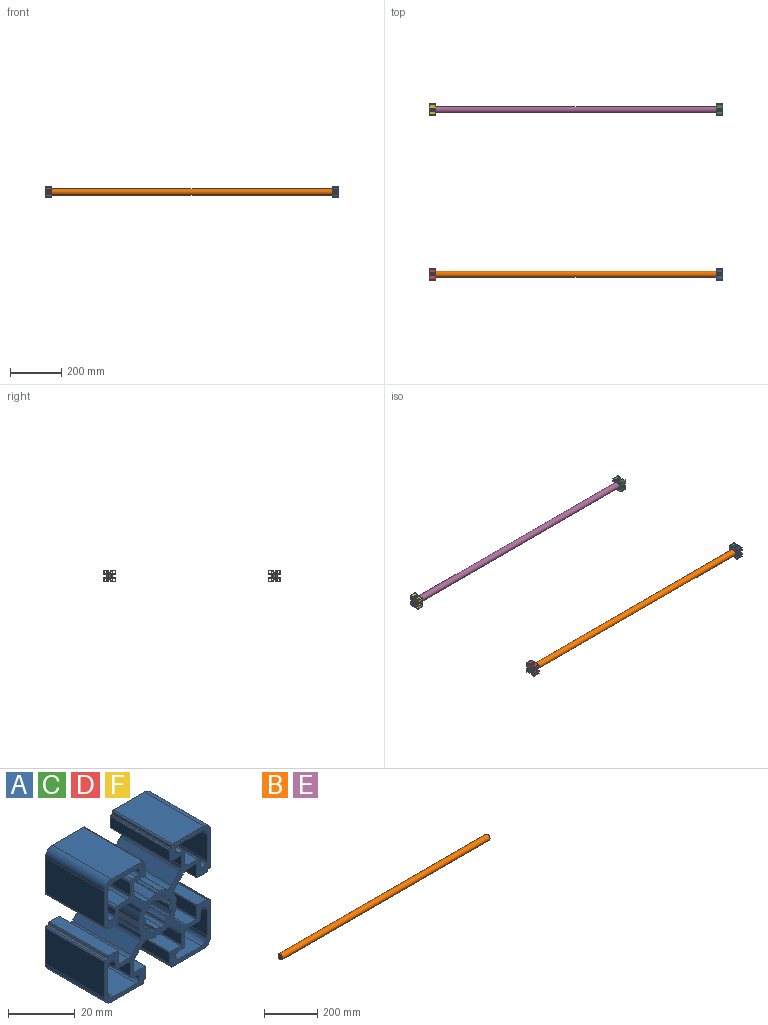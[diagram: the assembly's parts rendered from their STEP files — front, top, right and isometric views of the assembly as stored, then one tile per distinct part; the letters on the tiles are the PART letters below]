
ASSEMBLY  parts=6 mates=5
PART A: 246 faces, bbox 45x25x45 mm
  f0: plane 25x1.55mm, normal (0,0,1), area 38.7mm2, adj f1,f123,f244,f245
  f1: cylinder r=1mm len=25mm, axis (0,-1,0), area 39.3mm2, adj f0,f2,f244,f245
  f2: plane 25x4.45mm, normal (1,0,0), area 111.3mm2, adj f1,f3,f244,f245
  f3: cylinder r=1mm len=25mm, axis (0,-1,0), area 39.3mm2, adj f2,f4,f244,f245
  f4: plane 25x4.45mm, normal (0,0,1), area 111.3mm2, adj f3,f5,f244,f245
  f5: cylinder r=1mm len=25mm, axis (0,-1,0), area 39.3mm2, adj f4,f122,f244,f245
  f6: plane 25x1.55mm, normal (0,0,1), area 38.7mm2, adj f7,f129,f244,f245
  f7: cylinder r=1.5mm len=25mm, axis (0,-1,0), area 117.8mm2, adj f6,f8,f244,f245
  f8: plane 25x9.5mm, normal (0,0,-1), area 237.5mm2, adj f7,f9,f244,f245
  f9: cylinder r=2.5mm len=25mm, axis (0,-1,0), area 98.2mm2, adj f8,f10,f244,f245
  f10: plane 25x9.5mm, normal (1,0,0), area 237.5mm2, adj f9,f11,f244,f245
  f11: cylinder r=1.5mm len=25mm, axis (0,-1,0), area 117.8mm2, adj f10,f128,f244,f245
  f12: plane 25x9.5mm, normal (0,0,1), area 237.5mm2, adj f13,f135,f244,f245
  f13: cylinder r=1.5mm len=25mm, axis (0,-1,0), area 117.8mm2, adj f12,f14,f244,f245
  f14: plane 25x1.55mm, normal (0,0,-1), area 38.7mm2, adj f13,f15,f244,f245
  f15: cylinder r=1mm len=25mm, axis (0,-1,0), area 39.3mm2, adj f14,f16,f244,f245
  f16: plane 25x4.45mm, normal (-1,0,0), area 111.3mm2, adj f15,f17,f244,f245
  f17: cylinder r=1mm len=25mm, axis (0,-1,0), area 39.3mm2, adj f16,f134,f244,f245
  f18: plane 25x1.55mm, normal (0,0,-1), area 38.7mm2, adj f19,f141,f244,f245
  f19: cylinder r=1.5mm len=25mm, axis (0,-1,0), area 117.8mm2, adj f18,f20,f244,f245
  f20: plane 25x9.5mm, normal (0,0,1), area 237.5mm2, adj f19,f21,f244,f245
  f21: cylinder r=2.5mm len=25mm, axis (0,-1,0), area 98.2mm2, adj f20,f22,f244,f245
  f22: plane 25x9.5mm, normal (-1,0,0), area 237.5mm2, adj f21,f23,f244,f245
  f23: cylinder r=1.5mm len=25mm, axis (0,-1,0), area 117.8mm2, adj f22,f140,f244,f245
  f24: cylinder r=0.5mm len=25mm, axis (0,-1,0), area 21.3mm2, adj f25,f147,f244,f245
  f25: plane 25x0.46mm, normal (0.58,0,-0.82), area 14.2mm2, adj f24,f26,f244,f245
  f26: cylinder r=5mm len=25mm, axis (0,-1,0), area 43.5mm2, adj f25,f27,f244,f245
  f27: plane 25x0.48mm, normal (-0.82,0,0.57), area 14.5mm2, adj f26,f28,f244,f245
  f28: cylinder r=0.5mm len=25mm, axis (0,-1,0), area 21.2mm2, adj f27,f29,f244,f245
  f29: cylinder r=6.1mm len=25mm, axis (0,-1,0), area 39.3mm2, adj f28,f30,f244,f245
  f30: cylinder r=0.5mm len=25mm, axis (0,-1,0), area 21.3mm2, adj f29,f31,f244,f245
  f31: plane 25x0.57mm, normal (0.99,0,-0.17), area 14.4mm2, adj f30,f32,f244,f245
  f32: cylinder r=5mm len=25mm, axis (0,-1,0), area 44.6mm2, adj f31,f33,f244,f245
  f33: plane 25x0.57mm, normal (-0.99,0,-0.17), area 14.4mm2, adj f32,f34,f244,f245
  f34: cylinder r=0.5mm len=25mm, axis (0,-1,0), area 21.3mm2, adj f33,f35,f244,f245
  f35: cylinder r=6.1mm len=25mm, axis (0,-1,0), area 39.3mm2, adj f34,f36,f244,f245
  f36: cylinder r=0.5mm len=25mm, axis (0,-1,0), area 21.2mm2, adj f35,f37,f244,f245
  f37: plane 25x0.48mm, normal (0.82,0,0.57), area 14.5mm2, adj f36,f38,f244,f245
  f38: cylinder r=5mm len=25mm, axis (0,-1,0), area 43.5mm2, adj f37,f39,f244,f245
  f39: plane 25x0.46mm, normal (-0.58,0,-0.82), area 14.2mm2, adj f38,f40,f244,f245
  f40: cylinder r=0.5mm len=25mm, axis (0,-1,0), area 21.3mm2, adj f39,f41,f244,f245
  f41: cylinder r=6.1mm len=25mm, axis (0,-1,0), area 39.3mm2, adj f40,f42,f244,f245
  f42: cylinder r=0.5mm len=25mm, axis (0,-1,0), area 21.2mm2, adj f41,f43,f244,f245
  f43: plane 25x0.56mm, normal (0.18,0,0.98), area 14.1mm2, adj f42,f44,f244,f245
  f44: cylinder r=5mm len=25mm, axis (0,-1,0), area 43.6mm2, adj f43,f45,f244,f245
  f45: plane 25x0.56mm, normal (0.18,0,-0.98), area 14.1mm2, adj f44,f46,f244,f245
  f46: cylinder r=0.5mm len=25mm, axis (0,-1,0), area 21.2mm2, adj f45,f47,f244,f245
  f47: cylinder r=6.1mm len=25mm, axis (0,-1,0), area 39.3mm2, adj f46,f146,f244,f245
  f48: cylinder r=2mm len=25mm, axis (0,-1,0), area 61.2mm2, adj f49,f243,f244,f245
  f49: plane 25x3.57mm, normal (-0.71,0,-0.71), area 126.4mm2, adj f48,f50,f244,f245
  f50: cylinder r=2mm len=25mm, axis (0,-1,0), area 39.3mm2, adj f49,f51,f244,f245
  f51: plane 25x3.8mm, normal (0,0,-1), area 94.9mm2, adj f50,f52,f244,f245
  f52: cylinder r=0.2mm len=25mm, axis (0,-1,0), area 7.9mm2, adj f51,f53,f244,f245
  f53: plane 25x4.71mm, normal (1,0,0), area 117.6mm2, adj f52,f54,f244,f245
  f54: cylinder r=0.2mm len=25mm, axis (0,-1,0), area 7.9mm2, adj f53,f55,f244,f245
  f55: plane 25x4.03mm, normal (0,0,-1), area 100.8mm2, adj f54,f56,f244,f245
  f56: cylinder r=0.3mm len=25mm, axis (0,-1,0), area 11.8mm2, adj f55,f57,f244,f245
  f57: plane 25x0.28mm, normal (-1,0,0), area 6.9mm2, adj f56,f58,f244,f245
  f58: cylinder r=0.3mm len=25mm, axis (0,-1,0), area 11.8mm2, adj f57,f59,f244,f245
  f59: plane 25x0.7mm, normal (0,0,-1), area 17.5mm2, adj f58,f60,f244,f245
  f60: cylinder r=0.5mm len=25mm, axis (0,-1,0), area 19.6mm2, adj f59,f61,f244,f245
  f61: plane 25x13.12mm, normal (-1,0,0), area 328.1mm2, adj f60,f62,f244,f245
  f62: cylinder r=3mm len=25mm, axis (0,-1,0), area 117.8mm2, adj f61,f63,f244,f245
  f63: plane 25x13.2mm, normal (0,0,1), area 330mm2, adj f62,f64,f244,f245
  f64: cylinder r=0.5mm len=25mm, axis (0,-1,0), area 19.6mm2, adj f63,f65,f244,f245
  f65: plane 25x0.68mm, normal (1,0,0), area 17mm2, adj f64,f66,f244,f245
  f66: cylinder r=0.3mm len=25mm, axis (0,-1,0), area 11.8mm2, adj f65,f67,f244,f245
  f67: plane 25x0.2mm, normal (0,0,1), area 5mm2, adj f66,f68,f244,f245
  f68: cylinder r=0.3mm len=25mm, axis (0,-1,0), area 11.8mm2, adj f67,f69,f244,f245
  f69: plane 25x4mm, normal (1,0,0), area 100.1mm2, adj f68,f70,f244,f245
  f70: cylinder r=0.2mm len=25mm, axis (0,-1,0), area 7.9mm2, adj f69,f71,f244,f245
  f71: plane 25x4.59mm, normal (0,0,-1), area 114.9mm2, adj f70,f72,f244,f245
  f72: cylinder r=0.2mm len=25mm, axis (0,-1,0), area 7.9mm2, adj f71,f73,f244,f245
  f73: plane 25x3.81mm, normal (1,0,0), area 95.3mm2, adj f72,f74,f244,f245
  f74: cylinder r=1.94mm len=25mm, axis (0,-1,0), area 38.2mm2, adj f73,f75,f244,f245
  f75: plane 25x3.57mm, normal (0.71,0,0.71), area 126.1mm2, adj f74,f76,f244,f245
  f76: cylinder r=1.94mm len=25mm, axis (0,-1,0), area 60.8mm2, adj f75,f77,f244,f245
  f77: cylinder r=8mm len=25mm, axis (0,-1,0), area 70.7mm2, adj f76,f78,f244,f245
  f78: cylinder r=0.2mm len=25mm, axis (0,-1,0), area 3.2mm2, adj f77,f79,f244,f245
  f79: plane 25x0.75mm, normal (0.5,0,0.86), area 21.6mm2, adj f78,f80,f244,f245
  f80: cylinder r=0.2mm len=25mm, axis (0,-1,0), area 1.2mm2, adj f79,f81,f244,f245
  f81: cylinder r=0.2mm len=25mm, axis (0,-1,0), area 1.2mm2, adj f80,f82,f244,f245
  f82: plane 25x0.75mm, normal (-0.5,0,0.86), area 21.6mm2, adj f81,f83,f244,f245
  f83: cylinder r=0.2mm len=25mm, axis (0,-1,0), area 3.2mm2, adj f82,f84,f244,f245
  f84: cylinder r=8mm len=25mm, axis (0,-1,0), area 70.7mm2, adj f83,f85,f244,f245
  f85: cylinder r=1.94mm len=25mm, axis (0,-1,0), area 60.8mm2, adj f84,f86,f244,f245
  f86: plane 25x3.57mm, normal (-0.71,0,0.71), area 126.1mm2, adj f85,f87,f244,f245
  f87: cylinder r=1.94mm len=25mm, axis (0,-1,0), area 38.2mm2, adj f86,f88,f244,f245
  f88: plane 25x3.81mm, normal (-1,0,0), area 95.3mm2, adj f87,f89,f244,f245
  f89: cylinder r=0.2mm len=25mm, axis (0,-1,0), area 7.9mm2, adj f88,f90,f244,f245
  f90: plane 25x4.59mm, normal (0,0,-1), area 114.9mm2, adj f89,f91,f244,f245
  f91: cylinder r=0.2mm len=25mm, axis (0,-1,0), area 7.9mm2, adj f90,f92,f244,f245
  f92: plane 25x4mm, normal (-1,0,0), area 100.1mm2, adj f91,f93,f244,f245
  f93: cylinder r=0.3mm len=25mm, axis (0,-1,0), area 11.8mm2, adj f92,f94,f244,f245
  f94: plane 25x0.2mm, normal (0,0,1), area 5mm2, adj f93,f95,f244,f245
  f95: cylinder r=0.3mm len=25mm, axis (0,-1,0), area 11.8mm2, adj f94,f96,f244,f245
  f96: plane 25x0.68mm, normal (-1,0,0), area 17mm2, adj f95,f97,f244,f245
  f97: cylinder r=0.5mm len=25mm, axis (0,-1,0), area 19.6mm2, adj f96,f98,f244,f245
  f98: plane 25x13.2mm, normal (0,0,1), area 330mm2, adj f97,f99,f244,f245
  f99: cylinder r=3mm len=25mm, axis (0,-1,0), area 117.8mm2, adj f98,f100,f244,f245
  f100: plane 25x13.12mm, normal (1,0,0), area 328.1mm2, adj f99,f101,f244,f245
  f101: cylinder r=0.5mm len=25mm, axis (0,-1,0), area 19.6mm2, adj f100,f102,f244,f245
  f102: plane 25x0.7mm, normal (0,0,-1), area 17.5mm2, adj f101,f103,f244,f245
  f103: cylinder r=0.3mm len=25mm, axis (0,-1,0), area 11.8mm2, adj f102,f104,f244,f245
  f104: plane 25x0.28mm, normal (1,0,0), area 6.9mm2, adj f103,f105,f244,f245
  f105: cylinder r=0.3mm len=25mm, axis (0,-1,0), area 11.8mm2, adj f104,f106,f244,f245
  f106: plane 25x4.03mm, normal (0,0,-1), area 100.8mm2, adj f105,f107,f244,f245
  f107: cylinder r=0.2mm len=25mm, axis (0,-1,0), area 7.9mm2, adj f106,f108,f244,f245
  f108: plane 25x4.71mm, normal (-1,0,0), area 117.6mm2, adj f107,f109,f244,f245
  f109: cylinder r=0.2mm len=25mm, axis (0,-1,0), area 7.9mm2, adj f108,f110,f244,f245
  f110: plane 25x3.8mm, normal (0,0,-1), area 94.9mm2, adj f109,f111,f244,f245
  f111: cylinder r=2mm len=25mm, axis (0,-1,0), area 39.3mm2, adj f110,f112,f244,f245
  f112: plane 25x3.57mm, normal (0.71,0,-0.71), area 126.4mm2, adj f111,f113,f244,f245
  f113: cylinder r=2mm len=25mm, axis (0,-1,0), area 61.2mm2, adj f112,f114,f244,f245
  f114: cylinder r=8.05mm len=25mm, axis (0,-1,0), area 73.2mm2, adj f113,f115,f244,f245
  f115: cylinder r=0.2mm len=25mm, axis (0,-1,0), area 3.2mm2, adj f114,f116,f244,f245
  f116: plane 25x0.64mm, normal (0.87,0,-0.5), area 18.5mm2, adj f115,f117,f244,f245
  f117: cylinder r=0.2mm len=25mm, axis (0,-1,0), area 3.5mm2, adj f116,f118,f244,f245
  f118: cylinder r=0.2mm len=25mm, axis (0,-1,0), area 3.5mm2, adj f117,f119,f244,f245
  f119: plane 25x0.64mm, normal (0.87,0,0.5), area 18.5mm2, adj f118,f120,f244,f245
  f120: cylinder r=0.2mm len=25mm, axis (0,-1,0), area 3.2mm2, adj f119,f121,f244,f245
  f121: cylinder r=8.05mm len=25mm, axis (0,-1,0), area 73.2mm2, adj f120,f170,f244,f245
  f122: plane 25x1.55mm, normal (1,0,0), area 38.7mm2, adj f5,f127,f244,f245
  f123: cylinder r=1.5mm len=25mm, axis (0,-1,0), area 117.8mm2, adj f0,f124,f244,f245
  f124: plane 25x9.5mm, normal (0,0,-1), area 237.5mm2, adj f123,f125,f244,f245
  f125: cylinder r=2.5mm len=25mm, axis (0,-1,0), area 98.2mm2, adj f124,f126,f244,f245
  f126: plane 25x9.5mm, normal (-1,0,0), area 237.5mm2, adj f125,f127,f244,f245
  f127: cylinder r=1.5mm len=25mm, axis (0,-1,0), area 117.8mm2, adj f122,f126,f244,f245
  f128: plane 25x1.55mm, normal (-1,0,0), area 38.7mm2, adj f11,f133,f244,f245
  f129: cylinder r=1mm len=25mm, axis (0,-1,0), area 39.3mm2, adj f6,f130,f244,f245
  f130: plane 25x4.45mm, normal (-1,0,0), area 111.3mm2, adj f129,f131,f244,f245
  f131: cylinder r=1mm len=25mm, axis (0,-1,0), area 39.3mm2, adj f130,f132,f244,f245
  f132: plane 25x4.45mm, normal (0,0,1), area 111.3mm2, adj f131,f133,f244,f245
  f133: cylinder r=1mm len=25mm, axis (0,-1,0), area 39.3mm2, adj f128,f132,f244,f245
  f134: plane 25x4.45mm, normal (0,0,-1), area 111.3mm2, adj f17,f139,f244,f245
  f135: cylinder r=2.5mm len=25mm, axis (0,-1,0), area 98.2mm2, adj f12,f136,f244,f245
  f136: plane 25x9.5mm, normal (1,0,0), area 237.5mm2, adj f135,f137,f244,f245
  f137: cylinder r=1.5mm len=25mm, axis (0,-1,0), area 117.8mm2, adj f136,f138,f244,f245
  f138: plane 25x1.55mm, normal (-1,0,0), area 38.7mm2, adj f137,f139,f244,f245
  f139: cylinder r=1mm len=25mm, axis (0,-1,0), area 39.3mm2, adj f134,f138,f244,f245
  f140: plane 25x1.55mm, normal (1,0,0), area 38.7mm2, adj f23,f145,f244,f245
  f141: cylinder r=1mm len=25mm, axis (0,-1,0), area 39.3mm2, adj f18,f142,f244,f245
  f142: plane 25x4.45mm, normal (1,0,0), area 111.3mm2, adj f141,f143,f244,f245
  f143: cylinder r=1mm len=25mm, axis (0,-1,0), area 39.3mm2, adj f142,f144,f244,f245
  f144: plane 25x4.45mm, normal (0,0,-1), area 111.3mm2, adj f143,f145,f244,f245
  f145: cylinder r=1mm len=25mm, axis (0,-1,0), area 39.3mm2, adj f140,f144,f244,f245
  f146: cylinder r=0.5mm len=25mm, axis (0,-1,0), area 21.3mm2, adj f47,f169,f244,f245
  f147: cylinder r=6.1mm len=25mm, axis (0,-1,0), area 39.3mm2, adj f24,f148,f244,f245
  f148: cylinder r=0.5mm len=25mm, axis (0,-1,0), area 21.2mm2, adj f147,f149,f244,f245
  f149: plane 25x0.56mm, normal (-0.18,0,0.98), area 14.1mm2, adj f148,f150,f244,f245
  f150: cylinder r=5mm len=25mm, axis (0,-1,0), area 43.6mm2, adj f149,f151,f244,f245
  f151: plane 25x0.56mm, normal (-0.18,0,-0.98), area 14.1mm2, adj f150,f152,f244,f245
  f152: cylinder r=0.5mm len=25mm, axis (0,-1,0), area 21.2mm2, adj f151,f153,f244,f245
  f153: cylinder r=6.1mm len=25mm, axis (0,-1,0), area 39.3mm2, adj f152,f154,f244,f245
  f154: cylinder r=0.5mm len=25mm, axis (0,-1,0), area 21.3mm2, adj f153,f155,f244,f245
  f155: plane 25x0.46mm, normal (0.58,0,0.82), area 14.2mm2, adj f154,f156,f244,f245
  f156: cylinder r=5mm len=25mm, axis (0,-1,0), area 43.5mm2, adj f155,f157,f244,f245
  f157: plane 25x0.48mm, normal (-0.82,0,-0.57), area 14.5mm2, adj f156,f158,f244,f245
  f158: cylinder r=0.5mm len=25mm, axis (0,-1,0), area 21.2mm2, adj f157,f159,f244,f245
  f159: cylinder r=6.1mm len=25mm, axis (0,-1,0), area 39.3mm2, adj f158,f160,f244,f245
  f160: cylinder r=0.5mm len=25mm, axis (0,-1,0), area 21.3mm2, adj f159,f161,f244,f245
  f161: plane 25x0.57mm, normal (0.99,0,0.17), area 14.4mm2, adj f160,f162,f244,f245
  f162: cylinder r=5mm len=25mm, axis (0,-1,0), area 44.6mm2, adj f161,f163,f244,f245
  f163: plane 25x0.57mm, normal (-0.99,0,0.17), area 14.4mm2, adj f162,f164,f244,f245
  f164: cylinder r=0.5mm len=25mm, axis (0,-1,0), area 21.3mm2, adj f163,f165,f244,f245
  f165: cylinder r=6.1mm len=25mm, axis (0,-1,0), area 39.3mm2, adj f164,f166,f244,f245
  f166: cylinder r=0.5mm len=25mm, axis (0,-1,0), area 21.2mm2, adj f165,f167,f244,f245
  f167: plane 25x0.48mm, normal (0.82,0,-0.57), area 14.5mm2, adj f166,f168,f244,f245
  f168: cylinder r=5mm len=25mm, axis (0,-1,0), area 43.5mm2, adj f167,f169,f244,f245
  f169: plane 25x0.46mm, normal (-0.58,0,0.82), area 14.2mm2, adj f146,f168,f244,f245
  f170: cylinder r=2mm len=25mm, axis (0,-1,0), area 61.2mm2, adj f121,f171,f244,f245
  f171: plane 25x3.57mm, normal (0.71,0,0.71), area 126.4mm2, adj f170,f172,f244,f245
  f172: cylinder r=2mm len=25mm, axis (0,-1,0), area 39.3mm2, adj f171,f173,f244,f245
  f173: plane 25x3.8mm, normal (0,0,1), area 94.9mm2, adj f172,f174,f244,f245
  f174: cylinder r=0.2mm len=25mm, axis (0,-1,0), area 7.9mm2, adj f173,f175,f244,f245
  f175: plane 25x4.71mm, normal (-1,0,0), area 117.6mm2, adj f174,f176,f244,f245
  f176: cylinder r=0.2mm len=25mm, axis (0,-1,0), area 7.9mm2, adj f175,f177,f244,f245
  f177: plane 25x4.03mm, normal (0,0,1), area 100.8mm2, adj f176,f178,f244,f245
  f178: cylinder r=0.3mm len=25mm, axis (0,-1,0), area 11.8mm2, adj f177,f179,f244,f245
  f179: plane 25x0.28mm, normal (1,0,0), area 6.9mm2, adj f178,f180,f244,f245
  f180: cylinder r=0.3mm len=25mm, axis (0,-1,0), area 11.8mm2, adj f179,f181,f244,f245
  f181: plane 25x0.7mm, normal (0,0,1), area 17.5mm2, adj f180,f182,f244,f245
  f182: cylinder r=0.5mm len=25mm, axis (0,-1,0), area 19.6mm2, adj f181,f183,f244,f245
  f183: plane 25x13.12mm, normal (1,0,0), area 328.1mm2, adj f182,f184,f244,f245
  f184: cylinder r=3mm len=25mm, axis (0,-1,0), area 117.8mm2, adj f183,f185,f244,f245
  f185: plane 25x13.2mm, normal (0,0,-1), area 330mm2, adj f184,f186,f244,f245
  f186: cylinder r=0.5mm len=25mm, axis (0,-1,0), area 19.6mm2, adj f185,f187,f244,f245
  f187: plane 25x0.68mm, normal (-1,0,0), area 17mm2, adj f186,f188,f244,f245
  f188: cylinder r=0.3mm len=25mm, axis (0,-1,0), area 11.8mm2, adj f187,f189,f244,f245
  f189: plane 25x0.2mm, normal (0,0,-1), area 5mm2, adj f188,f190,f244,f245
  f190: cylinder r=0.3mm len=25mm, axis (0,-1,0), area 11.8mm2, adj f189,f191,f244,f245
  f191: plane 25x4mm, normal (-1,0,0), area 100.1mm2, adj f190,f192,f244,f245
  f192: cylinder r=0.2mm len=25mm, axis (0,-1,0), area 7.9mm2, adj f191,f193,f244,f245
  f193: plane 25x4.59mm, normal (0,0,1), area 114.9mm2, adj f192,f194,f244,f245
  f194: cylinder r=0.2mm len=25mm, axis (0,-1,0), area 7.9mm2, adj f193,f195,f244,f245
  f195: plane 25x3.81mm, normal (-1,0,0), area 95.3mm2, adj f194,f196,f244,f245
  f196: cylinder r=1.94mm len=25mm, axis (0,-1,0), area 38.2mm2, adj f195,f197,f244,f245
  f197: plane 25x3.57mm, normal (-0.71,0,-0.71), area 126.1mm2, adj f196,f198,f244,f245
  f198: cylinder r=1.94mm len=25mm, axis (0,-1,0), area 60.8mm2, adj f197,f199,f244,f245
  f199: cylinder r=8mm len=25mm, axis (0,-1,0), area 70.7mm2, adj f198,f200,f244,f245
  f200: cylinder r=0.2mm len=25mm, axis (0,-1,0), area 3.2mm2, adj f199,f201,f244,f245
  f201: plane 25x0.75mm, normal (-0.5,0,-0.86), area 21.6mm2, adj f200,f202,f244,f245
  f202: cylinder r=0.2mm len=25mm, axis (0,-1,0), area 1.2mm2, adj f201,f203,f244,f245
  f203: cylinder r=0.2mm len=25mm, axis (0,-1,0), area 1.2mm2, adj f202,f204,f244,f245
  f204: plane 25x0.75mm, normal (0.5,0,-0.86), area 21.6mm2, adj f203,f205,f244,f245
  f205: cylinder r=0.2mm len=25mm, axis (0,-1,0), area 3.2mm2, adj f204,f206,f244,f245
  f206: cylinder r=8mm len=25mm, axis (0,-1,0), area 70.7mm2, adj f205,f207,f244,f245
  f207: cylinder r=1.94mm len=25mm, axis (0,-1,0), area 60.8mm2, adj f206,f208,f244,f245
  f208: plane 25x3.57mm, normal (0.71,0,-0.71), area 126.1mm2, adj f207,f209,f244,f245
  f209: cylinder r=1.94mm len=25mm, axis (0,-1,0), area 38.2mm2, adj f208,f210,f244,f245
  f210: plane 25x3.81mm, normal (1,0,0), area 95.3mm2, adj f209,f211,f244,f245
  f211: cylinder r=0.2mm len=25mm, axis (0,-1,0), area 7.9mm2, adj f210,f212,f244,f245
  f212: plane 25x4.59mm, normal (0,0,1), area 114.9mm2, adj f211,f213,f244,f245
  f213: cylinder r=0.2mm len=25mm, axis (0,-1,0), area 7.9mm2, adj f212,f214,f244,f245
  f214: plane 25x4mm, normal (1,0,0), area 100.1mm2, adj f213,f215,f244,f245
  f215: cylinder r=0.3mm len=25mm, axis (0,-1,0), area 11.8mm2, adj f214,f216,f244,f245
  f216: plane 25x0.2mm, normal (0,0,-1), area 5mm2, adj f215,f217,f244,f245
  f217: cylinder r=0.3mm len=25mm, axis (0,-1,0), area 11.8mm2, adj f216,f218,f244,f245
  f218: plane 25x0.68mm, normal (1,0,0), area 17mm2, adj f217,f219,f244,f245
  f219: cylinder r=0.5mm len=25mm, axis (0,-1,0), area 19.6mm2, adj f218,f220,f244,f245
  f220: plane 25x13.2mm, normal (0,0,-1), area 330mm2, adj f219,f221,f244,f245
  f221: cylinder r=3mm len=25mm, axis (0,-1,0), area 117.8mm2, adj f220,f222,f244,f245
  f222: plane 25x13.12mm, normal (-1,0,0), area 328.1mm2, adj f221,f223,f244,f245
  f223: cylinder r=0.5mm len=25mm, axis (0,-1,0), area 19.6mm2, adj f222,f224,f244,f245
  f224: plane 25x0.7mm, normal (0,0,1), area 17.5mm2, adj f223,f225,f244,f245
  f225: cylinder r=0.3mm len=25mm, axis (0,-1,0), area 11.8mm2, adj f224,f226,f244,f245
  f226: plane 25x0.28mm, normal (-1,0,0), area 6.9mm2, adj f225,f227,f244,f245
  f227: cylinder r=0.3mm len=25mm, axis (0,-1,0), area 11.8mm2, adj f226,f228,f244,f245
  f228: plane 25x4.03mm, normal (0,0,1), area 100.8mm2, adj f227,f229,f244,f245
  f229: cylinder r=0.2mm len=25mm, axis (0,-1,0), area 7.9mm2, adj f228,f230,f244,f245
  f230: plane 25x4.71mm, normal (1,0,0), area 117.6mm2, adj f229,f231,f244,f245
  f231: cylinder r=0.2mm len=25mm, axis (0,-1,0), area 7.9mm2, adj f230,f232,f244,f245
  f232: plane 25x3.8mm, normal (0,0,1), area 94.9mm2, adj f231,f233,f244,f245
  f233: cylinder r=2mm len=25mm, axis (0,-1,0), area 39.3mm2, adj f232,f234,f244,f245
  f234: plane 25x3.57mm, normal (-0.71,0,0.71), area 126.4mm2, adj f233,f235,f244,f245
  f235: cylinder r=2mm len=25mm, axis (0,-1,0), area 61.2mm2, adj f234,f236,f244,f245
  f236: cylinder r=8.05mm len=25mm, axis (0,-1,0), area 73.2mm2, adj f235,f237,f244,f245
  f237: cylinder r=0.2mm len=25mm, axis (0,-1,0), area 3.2mm2, adj f236,f238,f244,f245
  f238: plane 25x0.64mm, normal (-0.87,0,0.5), area 18.5mm2, adj f237,f239,f244,f245
  f239: cylinder r=0.2mm len=25mm, axis (0,-1,0), area 3.5mm2, adj f238,f240,f244,f245
  f240: cylinder r=0.2mm len=25mm, axis (0,-1,0), area 3.5mm2, adj f239,f241,f244,f245
  f241: plane 25x0.64mm, normal (-0.87,0,-0.5), area 18.5mm2, adj f240,f242,f244,f245
  f242: cylinder r=0.2mm len=25mm, axis (0,-1,0), area 3.2mm2, adj f241,f243,f244,f245
  f243: cylinder r=8.05mm len=25mm, axis (0,-1,0), area 73.2mm2, adj f48,f242,f244,f245
  f244: plane 45x45mm, normal (0,-1,0), area 571.4mm2, adj f0,f1,f2,f3,f4,f5,f6,f7
  f245: plane 45x45mm, normal (0,1,0), area 571.4mm2, adj f0,f1,f2,f3,f4,f5,f6,f7
PART B: 3 faces, bbox 1100x25x25 mm
  f0: cylinder r=12.5mm len=1100mm, axis (-1,0,0), area 86393.8mm2, adj f1,f2
  f1: plane 25x25mm, normal (1,0,0), area 490.9mm2, adj f0
  f2: plane 25x25mm, normal (-1,0,0), area 490.9mm2, adj f0
PART C: same geometry as A
PART D: same geometry as A
PART E: same geometry as B
PART F: same geometry as A
PLACE A rot(axis=(-0.71,-0.71,0),180deg) t=(595.86,393.79,44.93)mm
PLACE B rot(axis=(1,0,0),180deg) t=(-529.14,393.76,44.98)mm
PLACE C rot(axis=(0,0,-1),90deg) t=(595.86,1038.74,45.01)mm
PLACE D rot(axis=(0.71,0.71,0),180deg) t=(-529.14,393.79,44.91)mm
PLACE E t=(-529.14,1038.76,44.96)mm
PLACE F rot(axis=(0,0,-1),90deg) t=(-529.14,1038.74,45.01)mm
MATE fastened D.f47 <-> B.f0  axis (-1,0,0) through (-529.14,393.76,44.98)mm
MATE fastened C.f26 <-> E.f0  axis (-1,0,0) through (570.86,1038.76,44.96)mm
MATE parallel F.f100 <-> D.f183  axis (0,-1,0) through (-541.64,1016.26,57.89)mm
MATE fastened A.f26 <-> B.f0  axis (-1,0,0) through (570.86,393.76,44.98)mm
MATE fastened F.f26 <-> E.f0  axis (-1,0,0) through (-529.14,1038.76,44.96)mm
